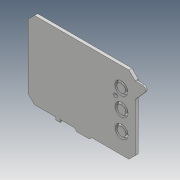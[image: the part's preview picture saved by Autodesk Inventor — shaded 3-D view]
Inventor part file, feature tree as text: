
AUTODESK INVENTOR PART (.ipt)
format: ipt  version: 2017 (Build 210142000, 142)  size: 415,232 bytes
history: native  units: mm
features: sketch x12, extrude x10, plane x2, other x2
ambient origin geometry x8: Origin, YZ Plane, XZ Plane, XY Plane, X Axis, Y Axis, Z Axis, Center Point
bodies: Solid1 (feature_tree)
feature tree (26):
  plane  "Work Plane2"
  sketch  "Sketch3"  dims[d27=2.0mm d28=2.0mm]
  plane  "Work Plane1"
  sketch  "Sketch4"  dims[d29=2.0mm d30=2.0mm]
  extrude  "Extrusion2"  Depth=2.0mm
  extrude  "Extrusion3"  Depth=2.0mm
  extrude  "Extrusion4"  Depth=2.0mm
  extrude  "Extrusion5"  Depth=2.0mm
  extrude  "Extrusion6"  Depth=2.0mm TaperAngle=0.0deg
  sketch  "Sketch9"  dims[d48=1.5mm d49=0.0mm d50=1.5mm]
  extrude  "Extrusion7"  Depth=1.5mm
  extrude  "Extrusion8"  Depth=1.5mm
  extrude  "Extrusion9"  Depth=22.0mm
  extrude  "Extrusion10"  Depth=0.5mm TaperAngle=0.0deg
  sketch  "Sketch14"  dims[d92=0.5mm d93=0.0mm]
  extrude  "Extrusion11"  Depth=1.0mm
  sketch  "Sketch6"  dims[d31=2.0mm d32=2.0mm]
  sketch  "Sketch7"  dims[d33=2.0mm d34=2.0mm]
  sketch  "Sketch8"  dims[d35=1.0mm d36=0.0mm d37=2.0mm d38=0.0mm]
  other  "Image5"
  other  "Image6"
  sketch  "Sketch10"  dims[d51=1.5mm d52=1.5mm]
  sketch  "Sketch11"  dims[d53=1.5mm d54=22.0mm]
  sketch  "Sketch12"  dims[d55=2.0mm d56=0.0mm d57=0.5mm d58=0.0mm]
  sketch  "Sketch13"  dims[d59=16.0mm d91=1.0mm]
  sketch  "Sketch15"  dims[d94=1.0mm d95=0.0mm d96=1.0mm d97=1.0mm d98=0.0mm d99=0.5mm d100=0.0mm d101=0.5mm d102=0.0mm]
